# Revit family: ДЗ-1-СO
name_source: partatom
category: Датчики
units: mm (PartAtom-declared; Revit-internal decimal feet)

## family parameters
Всегда вертикально = Да
На основе рабочей плоскости = Нет
Общий = Нет
При загрузке вырезать с полостями = Нет
Размер круглого соединителя = Использовать диаметр
Сохранять ориентацию аннотаций = Нет
Тип детали = Нормальный
Точка расчета площади = Да

## types (1)
- _АК_Газоанализатор
    ADSK_Группирование = АК_Газ
    ADSK_Единица измерения = шт.
    ADSK_Завод-изготовитель = ОВЕН
    ADSK_Код изделия = ДЗ-1-СО
    ADSK_Марка = ОВЕН ДЗ-1-СО
    ADSK_Масса = 0.1
    ADSK_Масса_Текст = 0.1
    ADSK_Материал = 05 Пластик ПВХ Белый
    ADSK_Наименование краткое = Датчик (сигнализатор) угарного газа: 
- Напряжение питания 230В~ ±10% 50Гц
- Потребляемая мощность 2 ВА
-1-й порог срабатывания 20 мг/м³ 
- 2-й порог срабатывания 100 мг/м³
Уровень громкости звукового сигнала 70дБ
- Выход реле 2х5А/250B~
- Степень защиты IP20
- Рабочая температура от -20 С до +70 С
    ADSK_Размер_Высота = 84 мм
    ADSK_Размер_Глубина = 36 мм
    ADSK_Размер_Ширина = 84 мм
    BE_Изображение 1 = Cable_3.png
    BE_Изображение 2 = QE_питание.png
    BE_Кабель (Наименование) = ППГнг(А)-HF 3x1,5 (D 10,9мм)
    BE_Крепеж (Наименование) = Держатель с защелкой (D 16 мм)
    BE_Линия конец (оборудование) = Щит
    BE_Линия начало (оборудование) = Газоанализатор, питание
    BE_Труба (Наименование) = Гофра 16 мм (Dвн 11,5мм)
    KKf.Примечание = Датчик угарного газа
    Степень защиты оболочки = IP67
